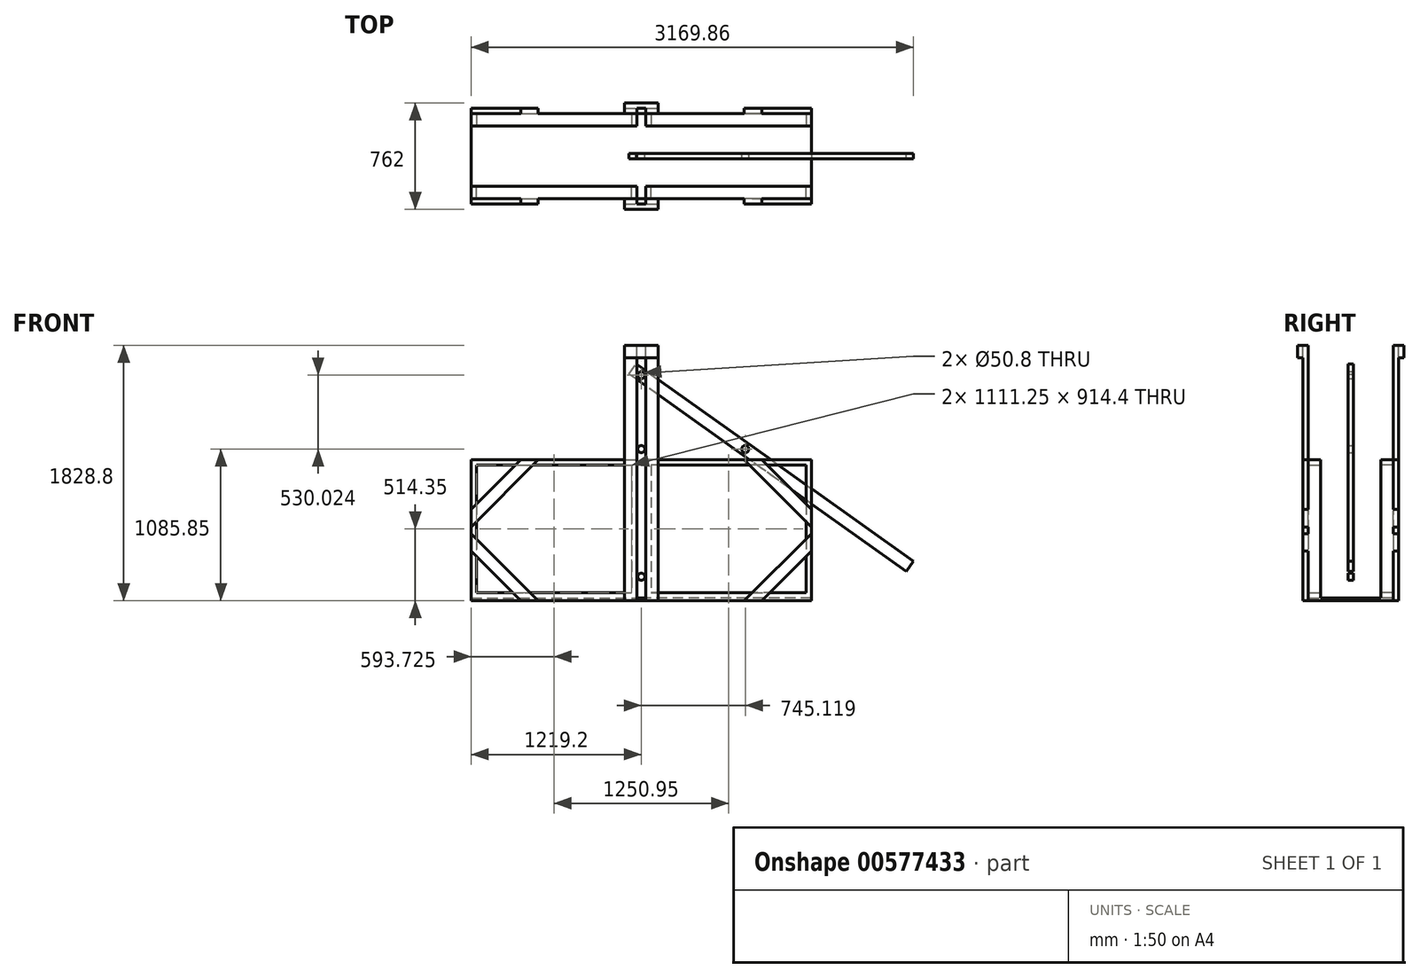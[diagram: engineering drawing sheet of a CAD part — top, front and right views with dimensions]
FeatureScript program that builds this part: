
annotation { "Feature Type Name" : "Feature", "Feature Type Description" : "" }
export const myFeature = defineFeature(function(context is Context, id is Id, definition is map)
    precondition{}
    {
        {
            var Q0;
            Q0=qCreatedBy(makeId("Top.planeOp"),FACE);
            var sketch = newSketch(context, id + "F0", { "sketchPlane" : qUnion([Q0])});
            skLineSegment(sketch, "E0.bottom", {"start": v(0, 0) * mm, "end": v(2438.4, 0) * mm});
            skLineSegment(sketch, "E0.top", {"start": v(0, -609.6) * mm, "end": v(2438.4, -609.6) * mm});
            skLineSegment(sketch, "E0.left", {"start": v(0, 0) * mm, "end": v(0, -609.6) * mm});
            skLineSegment(sketch, "E0.right", {"start": v(2438.4, 0) * mm, "end": v(2438.4, -609.6) * mm});
            skSolve(sketch);
        }
        {
            var Q0;
            Q0 = qSketchRegion(id + "F0", true);
            extrude(context, id + "F1", {"entities" : qUnion([Q0]), "depth" : 19.05 * mm, "offsetDistance" : 25.4 * mm});
        }
        {
            var Q0;
            Q0=makeQuery(id+"F1.opExtrude","CAP_FACE",FACE,{"disambiguationData":[OSD([sQuery(id+"F0.wireOp",EDGE,"E0.bottom"),sQuery(id+"F0.wireOp",EDGE,"E0.top"),sQuery(id+"F0.wireOp",EDGE,"E0.left"),sQuery(id+"F0.wireOp",EDGE,"E0.right")])],"isStart":false});
            var sketch = newSketch(context, id + "F2", { "sketchPlane" : qUnion([Q0])});
            skLineSegment(sketch, "E1.bottom", {"start": v(0, 0) * mm, "end": v(1187.45, 0) * mm});
            skLineSegment(sketch, "E1.top", {"start": v(0, -88.9) * mm, "end": v(1187.45, -88.9) * mm});
            skLineSegment(sketch, "E1.left", {"start": v(0, 0) * mm, "end": v(0, -88.9) * mm});
            skLineSegment(sketch, "E1.right", {"start": v(1187.45, 0) * mm, "end": v(1187.45, -88.9) * mm});
            skLineSegment(sketch, "E2", {"start": v(0, -304.8) * mm, "end": v(2438.4, -304.8) * mm, "construction": true});
            skLineSegment(sketch, "E3", {"start": v(1219.2, 0) * mm, "end": v(1219.2, -609.6) * mm, "construction": true});
            skLineSegment(sketch, "E4.MirrorCS", {"start": v(2438.4, -88.9) * mm, "end": v(1250.95, -88.9) * mm});
            skLineSegment(sketch, "E5.MirrorCS", {"start": v(2438.4, 0) * mm, "end": v(1250.95, 0) * mm});
            skLineSegment(sketch, "E6.MirrorCS", {"start": v(1250.95, 0) * mm, "end": v(1250.95, -88.9) * mm});
            skLineSegment(sketch, "E7.MirrorCS", {"start": v(2438.4, 0) * mm, "end": v(2438.4, -88.9) * mm});
            skLineSegment(sketch, "E8.MirrorCS", {"start": v(1187.45, -609.6) * mm, "end": v(1187.45, -520.7) * mm});
            skLineSegment(sketch, "E9.MirrorCS", {"start": v(0, -609.6) * mm, "end": v(1187.45, -609.6) * mm});
            skLineSegment(sketch, "E10.MirrorCS", {"start": v(0, -520.7) * mm, "end": v(1187.45, -520.7) * mm});
            skLineSegment(sketch, "E11.MirrorCS", {"start": v(0, -609.6) * mm, "end": v(0, -520.7) * mm});
            skLineSegment(sketch, "E12.MirrorCS", {"start": v(1250.95, -609.6) * mm, "end": v(1250.95, -520.7) * mm});
            skLineSegment(sketch, "E13.MirrorCS", {"start": v(2438.4, -520.7) * mm, "end": v(1250.95, -520.7) * mm});
            skLineSegment(sketch, "E14.MirrorCS", {"start": v(2438.4, -609.6) * mm, "end": v(1250.95, -609.6) * mm});
            skLineSegment(sketch, "E15.MirrorCS", {"start": v(2438.4, -609.6) * mm, "end": v(2438.4, -520.7) * mm});
            skSolve(sketch);
        }
        {
            var Q0;
            Q0 = qSketchRegion(id + "F2", true);
            extrude(context, id + "F3", {"entities" : qUnion([Q0]), "operationType" : NewBodyOperationType.ADD, "depth" : 38.1 * mm, "offsetDistance" : 25.4 * mm});
        }
        {
            var Q0;
            Q0=makeQuery(id+"F3.opExtrude","CAP_FACE",FACE,{"disambiguationData":[OSD([sQuery(id+"F2.wireOp",EDGE,"E1.bottom"),sQuery(id+"F2.wireOp",EDGE,"E1.top"),sQuery(id+"F2.wireOp",EDGE,"E1.left"),sQuery(id+"F2.wireOp",EDGE,"E1.right")])],"isStart":false});
            var sketch = newSketch(context, id + "F4", { "sketchPlane" : qUnion([Q0])});
            skLineSegment(sketch, "E16.bottom", {"start": v(0, 0) * mm, "end": v(38.1, 0) * mm});
            skLineSegment(sketch, "E16.top", {"start": v(0, -88.9) * mm, "end": v(38.1, -88.9) * mm});
            skLineSegment(sketch, "E16.left", {"start": v(0, 0) * mm, "end": v(0, -88.9) * mm});
            skLineSegment(sketch, "E16.right", {"start": v(38.1, 0) * mm, "end": v(38.1, -88.9) * mm});
            skLineSegment(sketch, "E17", {"start": v(0, -304.8) * mm, "end": v(2443.7, -304.8) * mm, "construction": true});
            skLineSegment(sketch, "E18", {"start": v(1219.2, 0) * mm, "end": v(1219.2, -609.6) * mm, "construction": true});
            skLineSegment(sketch, "E19", {"start": v(593.73, 0) * mm, "end": v(593.73, -88.9) * mm, "construction": true});
            skLineSegment(sketch, "E20.MirrorCS", {"start": v(1149.35, 0) * mm, "end": v(1149.35, -88.9) * mm});
            skLineSegment(sketch, "E21.MirrorCS", {"start": v(1187.45, 0) * mm, "end": v(1149.35, 0) * mm});
            skLineSegment(sketch, "E22.MirrorCS", {"start": v(1187.45, 0) * mm, "end": v(1187.45, -88.9) * mm});
            skLineSegment(sketch, "E23.MirrorCS", {"start": v(1187.45, -88.9) * mm, "end": v(1149.35, -88.9) * mm});
            skLineSegment(sketch, "E24.MirrorCS", {"start": v(1187.45, -609.6) * mm, "end": v(1187.45, -520.7) * mm});
            skLineSegment(sketch, "E25.MirrorCS", {"start": v(1187.45, -609.6) * mm, "end": v(1149.35, -609.6) * mm});
            skLineSegment(sketch, "E26.MirrorCS", {"start": v(1149.35, -609.6) * mm, "end": v(1149.35, -520.7) * mm});
            skLineSegment(sketch, "E27.MirrorCS", {"start": v(1187.45, -520.7) * mm, "end": v(1149.35, -520.7) * mm});
            skLineSegment(sketch, "E28.MirrorCS", {"start": v(38.1, -609.6) * mm, "end": v(38.1, -520.7) * mm});
            skLineSegment(sketch, "E29.MirrorCS", {"start": v(0, -609.6) * mm, "end": v(38.1, -609.6) * mm});
            skLineSegment(sketch, "E30.MirrorCS", {"start": v(0, -609.6) * mm, "end": v(0, -520.7) * mm});
            skLineSegment(sketch, "E31.MirrorCS", {"start": v(0, -520.7) * mm, "end": v(38.1, -520.7) * mm});
            skLineSegment(sketch, "E32.MirrorCS", {"start": v(1250.95, 0) * mm, "end": v(1250.95, -88.9) * mm});
            skLineSegment(sketch, "E33.MirrorCS", {"start": v(1250.95, 0) * mm, "end": v(1289.05, 0) * mm});
            skLineSegment(sketch, "E34.MirrorCS", {"start": v(1289.05, 0) * mm, "end": v(1289.05, -88.9) * mm});
            skLineSegment(sketch, "E35.MirrorCS", {"start": v(1250.95, -88.9) * mm, "end": v(1289.05, -88.9) * mm});
            skLineSegment(sketch, "E36.MirrorCS", {"start": v(1250.95, -609.6) * mm, "end": v(1250.95, -520.7) * mm});
            skLineSegment(sketch, "E37.MirrorCS", {"start": v(1250.95, -520.7) * mm, "end": v(1289.05, -520.7) * mm});
            skLineSegment(sketch, "E38.MirrorCS", {"start": v(1289.05, -609.6) * mm, "end": v(1289.05, -520.7) * mm});
            skLineSegment(sketch, "E39.MirrorCS", {"start": v(1250.95, -609.6) * mm, "end": v(1289.05, -609.6) * mm});
            skLineSegment(sketch, "E40.MirrorCS", {"start": v(2438.4, -609.6) * mm, "end": v(2400.3, -609.6) * mm});
            skLineSegment(sketch, "E41.MirrorCS", {"start": v(2438.4, -609.6) * mm, "end": v(2438.4, -520.7) * mm});
            skLineSegment(sketch, "E42.MirrorCS", {"start": v(2438.4, -520.7) * mm, "end": v(2400.3, -520.7) * mm});
            skLineSegment(sketch, "E43.MirrorCS", {"start": v(2400.3, -609.6) * mm, "end": v(2400.3, -520.7) * mm});
            skLineSegment(sketch, "E44.MirrorCS", {"start": v(2438.4, -88.9) * mm, "end": v(2400.3, -88.9) * mm});
            skLineSegment(sketch, "E45.MirrorCS", {"start": v(2438.4, 0) * mm, "end": v(2400.3, 0) * mm});
            skLineSegment(sketch, "E46.MirrorCS", {"start": v(2438.4, 0) * mm, "end": v(2438.4, -88.9) * mm});
            skLineSegment(sketch, "E47.MirrorCS", {"start": v(2400.3, 0) * mm, "end": v(2400.3, -88.9) * mm});
            skSolve(sketch);
        }
        {
            var Q0;
            Q0 = qSketchRegion(id + "F4", true);
            extrude(context, id + "F5", {"entities" : qUnion([Q0]), "operationType" : NewBodyOperationType.ADD, "depth" : 914.4 * mm, "offsetDistance" : 25.4 * mm});
        }
        {
            var Q0;
            Q0=makeQuery(id+"F5.opExtrude","CAP_FACE",FACE,{"disambiguationData":[OSD([sQuery(id+"F4.wireOp",EDGE,"E16.bottom"),sQuery(id+"F4.wireOp",EDGE,"E16.top"),sQuery(id+"F4.wireOp",EDGE,"E16.left"),sQuery(id+"F4.wireOp",EDGE,"E16.right")])],"isStart":false});
            var sketch = newSketch(context, id + "F6", { "sketchPlane" : qUnion([Q0])});
            skLineSegment(sketch, "E48.bottom", {"start": v(0, 0) * mm, "end": v(1187.45, 0) * mm});
            skLineSegment(sketch, "E48.top", {"start": v(0, -88.9) * mm, "end": v(1187.45, -88.9) * mm});
            skLineSegment(sketch, "E48.left", {"start": v(0, 0) * mm, "end": v(0, -88.9) * mm});
            skLineSegment(sketch, "E48.right", {"start": v(1187.45, 0) * mm, "end": v(1187.45, -88.9) * mm});
            skLineSegment(sketch, "E49", {"start": v(0, -304.8) * mm, "end": v(2439.86, -304.8) * mm, "construction": true});
            skLineSegment(sketch, "E50", {"start": v(1219.2, 0) * mm, "end": v(1219.2, -609.6) * mm, "construction": true});
            skLineSegment(sketch, "E51.MirrorCS", {"start": v(2438.4, 0) * mm, "end": v(1250.95, 0) * mm});
            skLineSegment(sketch, "E52.MirrorCS", {"start": v(2438.4, -88.9) * mm, "end": v(1250.95, -88.9) * mm});
            skLineSegment(sketch, "E53.MirrorCS", {"start": v(2438.4, 0) * mm, "end": v(2438.4, -88.9) * mm});
            skLineSegment(sketch, "E54.MirrorCS", {"start": v(1250.95, 0) * mm, "end": v(1250.95, -88.9) * mm});
            skLineSegment(sketch, "E55.MirrorCS", {"start": v(2438.4, -520.7) * mm, "end": v(1250.95, -520.7) * mm});
            skLineSegment(sketch, "E56.MirrorCS", {"start": v(2438.4, -609.6) * mm, "end": v(1250.95, -609.6) * mm});
            skLineSegment(sketch, "E57.MirrorCS", {"start": v(1187.45, -609.6) * mm, "end": v(1187.45, -520.7) * mm});
            skLineSegment(sketch, "E58.MirrorCS", {"start": v(0, -609.6) * mm, "end": v(0, -520.7) * mm});
            skLineSegment(sketch, "E59.MirrorCS", {"start": v(0, -520.7) * mm, "end": v(1187.45, -520.7) * mm});
            skLineSegment(sketch, "E60.MirrorCS", {"start": v(2438.4, -609.6) * mm, "end": v(2438.4, -520.7) * mm});
            skLineSegment(sketch, "E61.MirrorCS", {"start": v(1250.95, -609.6) * mm, "end": v(1250.95, -520.7) * mm});
            skLineSegment(sketch, "E62.MirrorCS", {"start": v(0, -609.6) * mm, "end": v(1187.45, -609.6) * mm});
            skSolve(sketch);
        }
        {
            var Q0;
            Q0 = qSketchRegion(id + "F6", true);
            extrude(context, id + "F7", {"entities" : qUnion([Q0]), "operationType" : NewBodyOperationType.ADD, "depth" : 38.1 * mm, "offsetDistance" : 25.4 * mm});
        }
        {
            var Q0;
            Q0=makeQuery(id+"F7.boolean.opBoolean","MERGE",FACE,{"derivedFrom":[makeQuery(id+"F5.boolean.opBoolean","MERGE",FACE,{"derivedFrom":[makeQuery(id+"F3.boolean.opBoolean","MERGE",FACE,{"derivedFrom":[makeQuery(id+"F1.opExtrude","SWEPT_FACE",FACE,{"disambiguationData":[OSD([sQuery(id+"F0.wireOp",EDGE,"E0.top")])]}),makeQuery(id+"F3.opExtrude","SWEPT_FACE",FACE,{"disambiguationData":[OSD([sQuery(id+"F2.wireOp",EDGE,"E9.MirrorCS")])]}),makeQuery(id+"F3.opExtrude","SWEPT_FACE",FACE,{"disambiguationData":[OSD([sQuery(id+"F2.wireOp",EDGE,"E14.MirrorCS")])]})]}),makeQuery(id+"F5.opExtrude","SWEPT_FACE",FACE,{"disambiguationData":[OSD([sQuery(id+"F4.wireOp",EDGE,"E25.MirrorCS")])]}),makeQuery(id+"F5.opExtrude","SWEPT_FACE",FACE,{"disambiguationData":[OSD([sQuery(id+"F4.wireOp",EDGE,"E29.MirrorCS")])]}),makeQuery(id+"F5.opExtrude","SWEPT_FACE",FACE,{"disambiguationData":[OSD([sQuery(id+"F4.wireOp",EDGE,"E39.MirrorCS")])]}),makeQuery(id+"F5.opExtrude","SWEPT_FACE",FACE,{"disambiguationData":[OSD([sQuery(id+"F4.wireOp",EDGE,"E40.MirrorCS")])]})]}),makeQuery(id+"F7.opExtrude","SWEPT_FACE",FACE,{"disambiguationData":[OSD([sQuery(id+"F6.wireOp",EDGE,"E56.MirrorCS")])]}),makeQuery(id+"F7.opExtrude","SWEPT_FACE",FACE,{"disambiguationData":[OSD([sQuery(id+"F6.wireOp",EDGE,"E62.MirrorCS")])]})]});
            var sketch = newSketch(context, id + "F8", { "sketchPlane" : qUnion([Q0])});
            skLineSegment(sketch, "E63.bottom", {"start": v(1250.95, 0) * mm, "end": v(1339.85, 0) * mm});
            skLineSegment(sketch, "E63.top", {"start": v(1250.95, 1828.8) * mm, "end": v(1339.85, 1828.8) * mm});
            skLineSegment(sketch, "E63.left", {"start": v(1250.95, 0) * mm, "end": v(1250.95, 1828.8) * mm});
            skLineSegment(sketch, "E63.right", {"start": v(1339.85, 0) * mm, "end": v(1339.85, 1828.8) * mm});
            skLineSegment(sketch, "E64", {"start": v(2082.8, 1009.65) * mm, "end": v(2438.4, 654.05) * mm});
            skLineSegment(sketch, "E65", {"start": v(2438.4, 654.05) * mm, "end": v(2438.4, 528.33) * mm});
            skLineSegment(sketch, "E66", {"start": v(2438.4, 528.33) * mm, "end": v(1957.08, 1009.65) * mm});
            skLineSegment(sketch, "E67", {"start": v(1957.08, 1009.65) * mm, "end": v(2082.8, 1009.65) * mm});
            skLineSegment(sketch, "E68", {"start": v(2438.4, 504.82) * mm, "end": v(0, 504.82) * mm, "construction": true});
            skLineSegment(sketch, "E69", {"start": v(1219.2, 0) * mm, "end": v(1219.2, 1299.12) * mm, "construction": true});
            skLineSegment(sketch, "E70.MirrorCS", {"start": v(2438.4, 481.32) * mm, "end": v(1957.08, 0) * mm});
            skLineSegment(sketch, "E71.MirrorCS", {"start": v(1957.08, 0) * mm, "end": v(2082.8, 0) * mm});
            skLineSegment(sketch, "E72.MirrorCS", {"start": v(2082.8, 0) * mm, "end": v(2438.4, 355.6) * mm});
            skLineSegment(sketch, "E73.MirrorCS", {"start": v(2438.4, 355.6) * mm, "end": v(2438.4, 481.32) * mm});
            skLineSegment(sketch, "E74.MirrorCS", {"start": v(355.6, 0) * mm, "end": v(0, 355.6) * mm});
            skLineSegment(sketch, "E75.MirrorCS", {"start": v(481.32, 0) * mm, "end": v(355.6, 0) * mm});
            skLineSegment(sketch, "E76.MirrorCS", {"start": v(0, 481.32) * mm, "end": v(481.32, 0) * mm});
            skLineSegment(sketch, "E77.MirrorCS", {"start": v(355.6, 1009.65) * mm, "end": v(0, 654.05) * mm});
            skLineSegment(sketch, "E78.MirrorCS", {"start": v(481.32, 1009.65) * mm, "end": v(355.6, 1009.65) * mm});
            skLineSegment(sketch, "E79.MirrorCS", {"start": v(0, 355.6) * mm, "end": v(0, 481.32) * mm});
            skLineSegment(sketch, "E80.MirrorCS", {"start": v(0, 654.05) * mm, "end": v(0, 528.33) * mm});
            skLineSegment(sketch, "E81.MirrorCS", {"start": v(0, 528.33) * mm, "end": v(481.32, 1009.65) * mm});
            skLineSegment(sketch, "E82.MirrorCS", {"start": v(1187.45, 1828.8) * mm, "end": v(1098.55, 1828.8) * mm});
            skLineSegment(sketch, "E83.MirrorCS", {"start": v(1187.45, 0) * mm, "end": v(1187.45, 1828.8) * mm});
            skLineSegment(sketch, "E84.MirrorCS", {"start": v(1098.55, 0) * mm, "end": v(1098.55, 1828.8) * mm});
            skLineSegment(sketch, "E85.MirrorCS", {"start": v(1187.45, 0) * mm, "end": v(1098.55, 0) * mm});
            skLineSegment(sketch, "E86.MirrorCS", {"start": v(0, 504.82) * mm, "end": v(2438.4, 504.82) * mm, "construction": true});
            skSolve(sketch);
        }
        {
            var Q0;
            Q0 = qSketchRegion(id + "F8", true);
            extrude(context, id + "F9", {"entities" : qUnion([Q0]), "operationType" : NewBodyOperationType.ADD, "depth" : 38.1 * mm, "offsetDistance" : 25.4 * mm});
        }
        {
            var Q0;
            Q0=makeQuery(id+"F7.boolean.opBoolean","MERGE",FACE,{"derivedFrom":[makeQuery(id+"F5.boolean.opBoolean","MERGE",FACE,{"derivedFrom":[makeQuery(id+"F3.boolean.opBoolean","MERGE",FACE,{"derivedFrom":[makeQuery(id+"F1.opExtrude","SWEPT_FACE",FACE,{"disambiguationData":[OSD([sQuery(id+"F0.wireOp",EDGE,"E0.bottom")])]}),makeQuery(id+"F3.opExtrude","SWEPT_FACE",FACE,{"disambiguationData":[OSD([sQuery(id+"F2.wireOp",EDGE,"E1.bottom")])]}),makeQuery(id+"F3.opExtrude","SWEPT_FACE",FACE,{"disambiguationData":[OSD([sQuery(id+"F2.wireOp",EDGE,"E5.MirrorCS")])]})]}),makeQuery(id+"F5.opExtrude","SWEPT_FACE",FACE,{"disambiguationData":[OSD([sQuery(id+"F4.wireOp",EDGE,"E16.bottom")])]}),makeQuery(id+"F5.opExtrude","SWEPT_FACE",FACE,{"disambiguationData":[OSD([sQuery(id+"F4.wireOp",EDGE,"E21.MirrorCS")])]}),makeQuery(id+"F5.opExtrude","SWEPT_FACE",FACE,{"disambiguationData":[OSD([sQuery(id+"F4.wireOp",EDGE,"E33.MirrorCS")])]}),makeQuery(id+"F5.opExtrude","SWEPT_FACE",FACE,{"disambiguationData":[OSD([sQuery(id+"F4.wireOp",EDGE,"E45.MirrorCS")])]})]}),makeQuery(id+"F7.opExtrude","SWEPT_FACE",FACE,{"disambiguationData":[OSD([sQuery(id+"F6.wireOp",EDGE,"E48.bottom")])]}),makeQuery(id+"F7.opExtrude","SWEPT_FACE",FACE,{"disambiguationData":[OSD([sQuery(id+"F6.wireOp",EDGE,"E51.MirrorCS")])]})]});
            var sketch = newSketch(context, id + "F10", { "sketchPlane" : qUnion([Q0])});
            skLineSegment(sketch, "E87.bottom", {"start": v(-1187.45, 0) * mm, "end": v(-1098.55, 0) * mm});
            skLineSegment(sketch, "E87.top", {"start": v(-1187.45, 1828.8) * mm, "end": v(-1098.55, 1828.8) * mm});
            skLineSegment(sketch, "E87.left", {"start": v(-1187.45, 0) * mm, "end": v(-1187.45, 1828.8) * mm});
            skLineSegment(sketch, "E87.right", {"start": v(-1098.55, 0) * mm, "end": v(-1098.55, 1828.8) * mm});
            skLineSegment(sketch, "E88", {"start": v(-355.6, 1009.65) * mm, "end": v(0, 654.05) * mm});
            skLineSegment(sketch, "E89", {"start": v(0, 654.05) * mm, "end": v(0, 528.33) * mm});
            skLineSegment(sketch, "E90", {"start": v(0, 528.33) * mm, "end": v(-481.32, 1009.65) * mm});
            skLineSegment(sketch, "E91", {"start": v(-481.32, 1009.65) * mm, "end": v(-355.6, 1009.65) * mm});
            skLineSegment(sketch, "E92", {"start": v(0, 504.83) * mm, "end": v(-2438.4, 504.82) * mm, "construction": true});
            skLineSegment(sketch, "E93", {"start": v(-1219.2, -181.13) * mm, "end": v(-1219.2, 1118) * mm, "construction": true});
            skLineSegment(sketch, "E94.MirrorCS", {"start": v(0, 481.32) * mm, "end": v(-481.32, 0) * mm});
            skLineSegment(sketch, "E95.MirrorCS", {"start": v(-481.32, 0) * mm, "end": v(-355.6, 0) * mm});
            skLineSegment(sketch, "E96.MirrorCS", {"start": v(-355.6, 0) * mm, "end": v(0, 355.6) * mm});
            skLineSegment(sketch, "E97.MirrorCS", {"start": v(0, 355.6) * mm, "end": v(0, 481.32) * mm});
            skLineSegment(sketch, "E98.MirrorCS", {"start": v(-2082.8, 0) * mm, "end": v(-2438.4, 355.6) * mm});
            skLineSegment(sketch, "E99.MirrorCS", {"start": v(-1957.08, 0) * mm, "end": v(-2082.8, 0) * mm});
            skLineSegment(sketch, "E100.MirrorCS", {"start": v(-2438.4, 481.32) * mm, "end": v(-1957.08, 0) * mm});
            skLineSegment(sketch, "E101.MirrorCS", {"start": v(-2082.8, 1009.65) * mm, "end": v(-2438.4, 654.05) * mm});
            skLineSegment(sketch, "E102.MirrorCS", {"start": v(-1957.08, 1009.65) * mm, "end": v(-2082.8, 1009.65) * mm});
            skLineSegment(sketch, "E103.MirrorCS", {"start": v(-2438.4, 355.6) * mm, "end": v(-2438.4, 481.32) * mm});
            skLineSegment(sketch, "E104.MirrorCS", {"start": v(-2438.4, 654.05) * mm, "end": v(-2438.4, 528.33) * mm});
            skLineSegment(sketch, "E105.MirrorCS", {"start": v(-2438.4, 528.33) * mm, "end": v(-1957.08, 1009.65) * mm});
            skLineSegment(sketch, "E106.MirrorCS", {"start": v(-1250.95, 1828.8) * mm, "end": v(-1339.85, 1828.8) * mm});
            skLineSegment(sketch, "E107.MirrorCS", {"start": v(-1250.95, 0) * mm, "end": v(-1250.95, 1828.8) * mm});
            skLineSegment(sketch, "E108.MirrorCS", {"start": v(-1339.85, 0) * mm, "end": v(-1339.85, 1828.8) * mm});
            skLineSegment(sketch, "E109.MirrorCS", {"start": v(-1250.95, 0) * mm, "end": v(-1339.85, 0) * mm});
            skLineSegment(sketch, "E110.MirrorCS", {"start": v(-2438.4, 504.82) * mm, "end": v(0, 504.83) * mm, "construction": true});
            skSolve(sketch);
        }
        {
            var Q0;
            Q0 = qSketchRegion(id + "F10", true);
            extrude(context, id + "F11", {"entities" : qUnion([Q0]), "operationType" : NewBodyOperationType.ADD, "depth" : 38.1 * mm, "offsetDistance" : 25.4 * mm});
        }
        {
            var Q0;
            Q0=makeQuery(id+"F11.opExtrude","CAP_FACE",FACE,{"disambiguationData":[OSD([sQuery(id+"F10.wireOp",EDGE,"E106.MirrorCS"),sQuery(id+"F10.wireOp",EDGE,"E107.MirrorCS"),sQuery(id+"F10.wireOp",EDGE,"E108.MirrorCS"),sQuery(id+"F10.wireOp",EDGE,"E109.MirrorCS")])],"isStart":false});
            var sketch = newSketch(context, id + "F12", { "sketchPlane" : qUnion([Q0])});
            skLineSegment(sketch, "E111.bottom", {"start": v(-1339.85, 1828.8) * mm, "end": v(-1098.55, 1828.8) * mm});
            skLineSegment(sketch, "E111.top", {"start": v(-1339.85, 1739.9) * mm, "end": v(-1098.55, 1739.9) * mm});
            skLineSegment(sketch, "E111.left", {"start": v(-1339.85, 1828.8) * mm, "end": v(-1339.85, 1739.9) * mm});
            skLineSegment(sketch, "E111.right", {"start": v(-1098.55, 1828.8) * mm, "end": v(-1098.55, 1739.9) * mm});
            skSolve(sketch);
        }
        {
            var Q0;
            Q0 = qSketchRegion(id + "F12", true);
            extrude(context, id + "F13", {"entities" : qUnion([Q0]), "operationType" : NewBodyOperationType.ADD, "depth" : 38.1 * mm, "offsetDistance" : 25.4 * mm});
        }
        {
            var Q0;
            Q0=makeQuery(id+"F9.opExtrude","CAP_FACE",FACE,{"disambiguationData":[OSD([sQuery(id+"F8.wireOp",EDGE,"E82.MirrorCS"),sQuery(id+"F8.wireOp",EDGE,"E83.MirrorCS"),sQuery(id+"F8.wireOp",EDGE,"E84.MirrorCS"),sQuery(id+"F8.wireOp",EDGE,"E85.MirrorCS")])],"isStart":false});
            var sketch = newSketch(context, id + "F14", { "sketchPlane" : qUnion([Q0])});
            skLineSegment(sketch, "E112.bottom", {"start": v(1098.55, 1828.8) * mm, "end": v(1339.85, 1828.8) * mm});
            skLineSegment(sketch, "E112.top", {"start": v(1098.55, 1739.9) * mm, "end": v(1339.85, 1739.9) * mm});
            skLineSegment(sketch, "E112.left", {"start": v(1098.55, 1828.8) * mm, "end": v(1098.55, 1739.9) * mm});
            skLineSegment(sketch, "E112.right", {"start": v(1339.85, 1828.8) * mm, "end": v(1339.85, 1739.9) * mm});
            skSolve(sketch);
        }
        {
            var Q0;
            Q0 = qSketchRegion(id + "F14", true);
            extrude(context, id + "F15", {"entities" : qUnion([Q0]), "operationType" : NewBodyOperationType.ADD, "depth" : 38.1 * mm, "offsetDistance" : 25.4 * mm});
        }
        {
            var Q0;
            {var subQ1=sQuery(id+"F10.wireOp",EDGE,"E106.MirrorCS");var subQ2=sQuery(id+"F10.wireOp",EDGE,"E108.MirrorCS");var subQ4=sQuery(id+"F10.wireOp",EDGE,"E107.MirrorCS");Q0=makeQuery(id+"F11.boolean.opBoolean","SPLIT",FACE,{"disambiguationData":[TD([makeQuery(id+"F3.opExtrude","SWEPT_FACE",FACE,{"disambiguationData":[OSD([sQuery(id+"F2.wireOp",EDGE,"E6.MirrorCS")])]})])],"derivedFrom":makeQuery(id+"F11.opExtrude","CAP_FACE",FACE,{"disambiguationData":[OSD([subQ1,subQ4,subQ2,sQuery(id+"F10.wireOp",EDGE,"E109.MirrorCS")])],"isStart":true})});}
            cPlane(context, id + "F16", {"entities" : qUnion([Q0]), "cplaneType" : CPlaneType.OFFSET, "offset" : 304.8 * mm, "width" : 152.4 * mm, "height" : 152.4 * mm});
        }
        {
            var Q0;
            Q0=qCreatedBy(id+"F16.planeOp",FACE);
            var sketch = newSketch(context, id + "F17", { "sketchPlane" : qUnion([Q0])});
            skLineSegment(sketch, "E113", {"start": v(1182.87, 1696.26) * mm, "end": v(3169.86, 282.87) * mm});
            skLineSegment(sketch, "E114", {"start": v(3169.86, 282.87) * mm, "end": v(3118.33, 210.42) * mm});
            skLineSegment(sketch, "E115", {"start": v(3118.33, 210.42) * mm, "end": v(1131.34, 1623.82) * mm});
            skLineSegment(sketch, "E116", {"start": v(1131.34, 1623.82) * mm, "end": v(1182.87, 1696.26) * mm});
            skCircle(sketch, "E117", {"center": v(1219.2, 1615.87) * mm, "radius": 25.4 * mm});
            skCircle(sketch, "E118", {"center": v(1964.32, 1085.85) * mm, "radius": 25.4 * mm});
            skCircle(sketch, "E119", {"center": v(1219.2, 1085.85) * mm, "radius": 25.4 * mm});
            skLineSegment(sketch, "E120", {"start": v(1219.2, 0) * mm, "end": v(1219.2, 1933.95) * mm, "construction": true});
            skCircle(sketch, "E121", {"center": v(1219.2, 171.45) * mm, "radius": 25.4 * mm});
            skSolve(sketch);
        }
        {
            var Q0;
            Q0 = qSketchRegion(id + "F17", true);
            extrude(context, id + "F18", {"entities" : qUnion([Q0]), "endBound" : BoundingType.SYMMETRIC, "depth" : 38.1 * mm, "offsetDistance" : 25.4 * mm});
        }
    });
